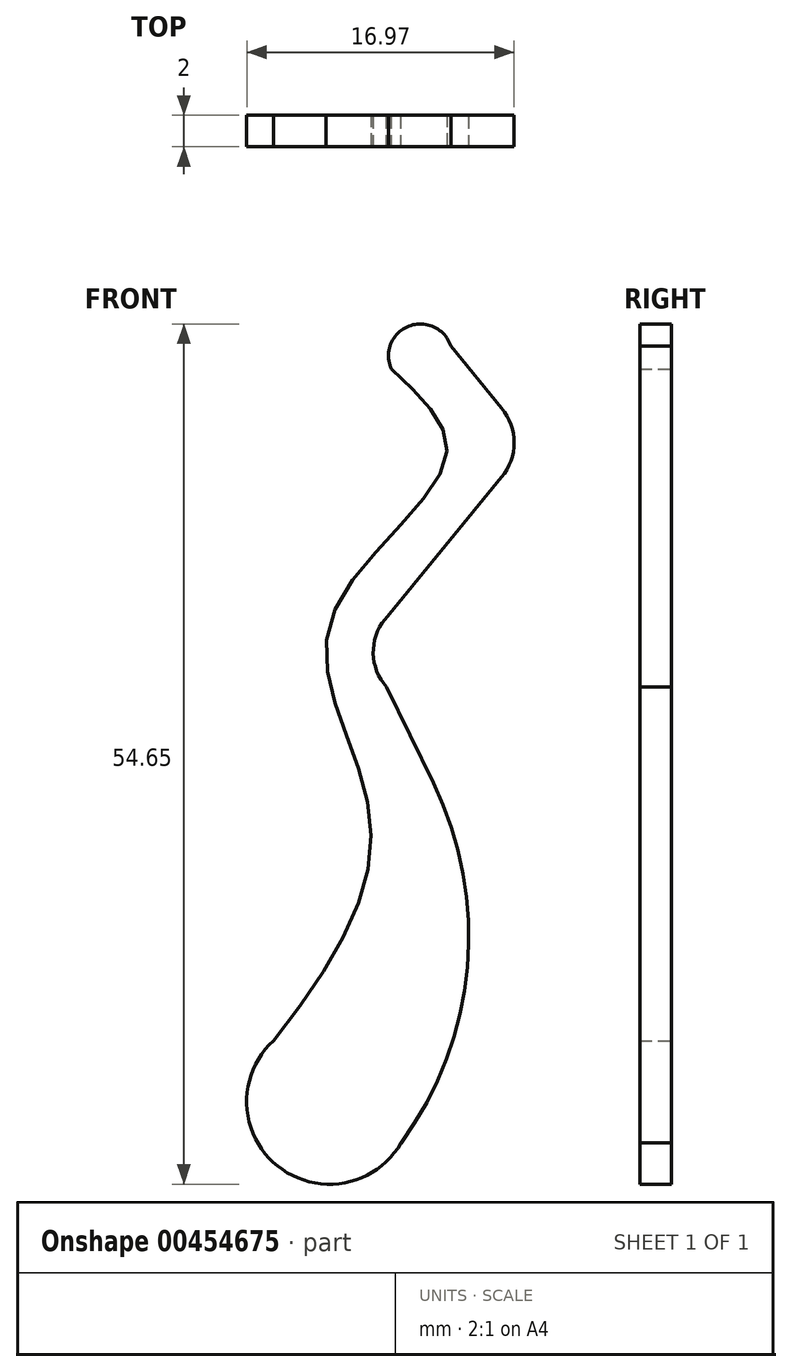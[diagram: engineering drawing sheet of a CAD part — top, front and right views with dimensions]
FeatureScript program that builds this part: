
annotation { "Feature Type Name" : "Feature", "Feature Type Description" : "" }
export const myFeature = defineFeature(function(context is Context, id is Id, definition is map)
    precondition{}
    {
        {
            var Q0;
            Q0=qCreatedBy(makeId("Front.planeOp"),FACE);
            var sketch = newSketch(context, id + "F0", { "sketchPlane" : qUnion([Q0])});
            skCircle(sketch, "E0", {"center": v(0, 0) * mm, "radius": 5.25 * mm});
            skFitSpline(sketch, "E1", {"points": [v(-4.51, 2.7) * mm, v(2.6, 17.8) * mm, v(0, 30.3) * mm, v(7.36, 40.71) * mm, v(3.94, 46.51) * mm], "startDerivative": vector(43.23, 52.27) * mm, "endDerivative": vector(-32.04, 29.5) * mm});
            skArc(sketch, "E2", {"start": v(7.7, 47.99) * mm, "mid": v(5.04, 49.26) * mm, "end": v(3.94, 46.51) * mm});
            skLineSegment(sketch, "E3", {"start": v(7.7, 47.99) * mm, "end": v(10.94, 44.05) * mm});
            skArc(sketch, "E4", {"start": v(10.94, 39.66) * mm, "mid": v(11.72, 41.85) * mm, "end": v(10.94, 44.05) * mm});
            skLineSegment(sketch, "E5", {"start": v(10.94, 39.66) * mm, "end": v(3.53, 30.64) * mm});
            skArc(sketch, "E6", {"start": v(3.53, 30.64) * mm, "mid": v(2.78, 28.47) * mm, "end": v(3.62, 26.34) * mm});
            skLineSegment(sketch, "E7", {"start": v(3.62, 26.34) * mm, "end": v(6.6, 20.24) * mm});
            skArc(sketch, "E8", {"start": v(3.63, -3.8) * mm, "mid": v(8.68, 7.78) * mm, "end": v(6.6, 20.24) * mm});
            skSolve(sketch);
        }
        {
            var Q0;
            Q0 = qSketchRegion(id + "F0", true);
            extrude(context, id + "F1", {"entities" : qUnion([Q0]), "depth" : 2 * mm, "offsetDistance" : 25 * mm});
        }
    });
